MODEL slx_3adbd9916a3d
BLOCK [Scope] Scope
  DataFormat = StructureWithTime
  Floating = off
  NumInputPorts = 1
  Ports = [1]
  SampleTime = 0
  ShowLegends = off
BLOCK [Scope] Scope1
  DataFormat = StructureWithTime
  Floating = off
  NumInputPorts = 1
  Ports = [1]
  SampleTime = 0
  SaveName = ScopeData1
  ShowLegends = off
BLOCK [SubSystem] Subsystem
  Ports = [0, 2]
  RequestExecContextInheritance = off
BLOCK [Integrator] Subsystem/Integrator
  Ports = [1, 1]
BLOCK [Integrator] Subsystem/Integrator1
  Ports = [1, 1]
BLOCK [Integrator] Subsystem/Integrator2
  Ports = [1, 1]
BLOCK [Integrator] Subsystem/Integrator3
  InitialCondition = 0.5
  Ports = [1, 1]
BLOCK [SubSystem] Subsystem/MATLAB Function
  ErrorFcn = Stateflow.Translate.translate
  PermitHierarchicalResolution = ExplicitOnly
  Ports = [4, 1]
  RequestExecContextInheritance = off
  SFBlockType = MATLAB Function
  TreatAsAtomicUnit = on
BLOCK [Demux] Subsystem/MATLAB Function/ Demux 
  Outputs = 1
  Ports = [1, 1]
BLOCK [S-Function] Subsystem/MATLAB Function/ SFunction 
  EnableBusSupport = on
  FunctionName = sf_sfun
  PortCounts = [4 2]
  Ports = [4, 2]
  Tag = Stateflow S-Function equ_diff 2
BLOCK [Terminator] Subsystem/MATLAB Function/ Terminator 
BLOCK [Outport] Subsystem/MATLAB Function/F
  IconDisplay = Port number
BLOCK [Inport] Subsystem/MATLAB Function/alpha
  IconDisplay = Port number
  Port = 3
BLOCK [Inport] Subsystem/MATLAB Function/alphadot
  IconDisplay = Port number
  Port = 4
BLOCK [Inport] Subsystem/MATLAB Function/x
  IconDisplay = Port number
BLOCK [Inport] Subsystem/MATLAB Function/xdot
  IconDisplay = Port number
  Port = 2
BLOCK [Mux] Subsystem/Mux
  DisplayOption = bar
  Ports = [4, 1]
BLOCK [Mux] Subsystem/Mux1
  DisplayOption = bar
  Inputs = 3
  Ports = [3, 1]
BLOCK [Outport] Subsystem/Out1
  IconDisplay = Port number
BLOCK [Outport] Subsystem/Out2
  IconDisplay = Port number
  Port = 2
BLOCK [Fcn] Subsystem/alphaddot
  Expr = sin(u(1))*u(2)/lp+g/lp*sin(u(1))-cos(u(1))*u(3)/lp
BLOCK [Fcn] Subsystem/xddot
  Expr = u(4)-mp*lp+(mp+mc)*u(3)*cos(u(1))-mp*lp/(mp+mc)*u(2)^2*sin(u(1))
BLOCK [Outport] angle
  IconDisplay = Port number
  Port = 2
BLOCK [Outport] position
  IconDisplay = Port number
LINE Subsystem/Integrator1:1 -> Subsystem/Integrator3:1
LINE Subsystem/Integrator1:1 -> Subsystem/MATLAB Function:4
LINE Subsystem/Integrator1:1 -> Subsystem/Mux1:2
LINE Subsystem/Integrator1:1 -> Subsystem/Mux:2
LINE Subsystem/Integrator2:1 -> Subsystem/MATLAB Function:1
LINE Subsystem/Integrator2:1 -> Subsystem/Out1:1
LINE Subsystem/Integrator3:1 -> Subsystem/MATLAB Function:3
LINE Subsystem/Integrator3:1 -> Subsystem/Mux1:1
LINE Subsystem/Integrator3:1 -> Subsystem/Mux:1
LINE Subsystem/Integrator3:1 -> Subsystem/Out2:1
LINE Subsystem/Integrator:1 -> Subsystem/Integrator2:1
LINE Subsystem/Integrator:1 -> Subsystem/MATLAB Function:2
LINE Subsystem/MATLAB Function:1 -> Subsystem/Mux:4
LINE Subsystem/Mux1:1 -> Subsystem/alphaddot:1
LINE Subsystem/Mux:1 -> Subsystem/xddot:1
LINE Subsystem/alphaddot:1 -> Subsystem/Integrator1:1
LINE Subsystem/alphaddot:1 -> Subsystem/Mux:3
LINE Subsystem/xddot:1 -> Subsystem/Integrator:1
LINE Subsystem/xddot:1 -> Subsystem/Mux1:3
LINE Subsystem:1 -> Scope:1
LINE Subsystem:1 -> position:1
LINE Subsystem:2 -> Scope1:1
LINE Subsystem:2 -> angle:1
